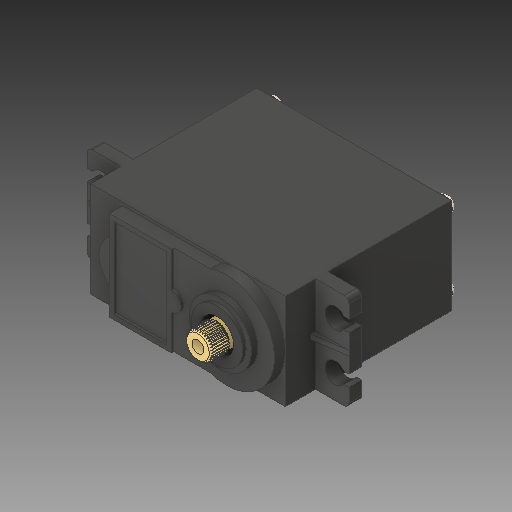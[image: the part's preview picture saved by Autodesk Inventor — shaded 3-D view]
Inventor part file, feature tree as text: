
AUTODESK INVENTOR PART (.ipt)
format: ipt  version: 2020 (Build 240168000, 168)  size: 561,664 bytes
history: mixed  units: mm
features: projected_geometry x4, other x1, sketch x1, mirror x1, imported_body x1
ambient origin geometry x8: Origin, YZ Plane, XZ Plane, XY Plane, X Axis, Y Axis, Z Axis, Center Point
bodies: Body1 (imported_parasolid)
feature tree (8):
  other  "Твердое тело1"
  sketch  "Эскиз1"
  projected_geometry  "Спроецированная петля1"
  projected_geometry  "Спроецированная петля2"
  projected_geometry  "Спроецированная петля3"
  projected_geometry  "Спроецированная петля4"
  mirror  "Mirror4"
  imported_body  NMx_Import_Brep_tag  [imported B-rep: ~118 faces, bbox_mm=[54.7, 20.0, 39.0]]
